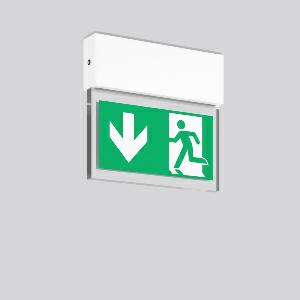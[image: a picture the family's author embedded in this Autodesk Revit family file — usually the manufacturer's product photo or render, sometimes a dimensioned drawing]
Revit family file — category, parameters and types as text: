
# Revit family: halyxx_671736_002_1_639e
name_source: partatom
category: Lighting Fixtures
units: mm (PartAtom-declared; Revit-internal decimal feet)

## family parameters
Cut with Voids When Loaded = No
Host = Face
Light Source = No
Part Type = Normal
Room Calculation Point = No
Round Connector Dimension = Use Diameter
Shared = No

## types (1)
- HALYXX (1 x LED Modul 840, 60 lm, 4000)
    Apparent Load = 2 VA
    Approval mark = CE
    CIE Flux Codes = 18 46 76 54 100
    Color Rendering = 80
    Color Temperature = 4000
    Default Elevation = 1800 mm
    Description = Series: HALYXX
Luminaire for escape route identification. Housing: extruded aluminium profile, anodised or powder-coated. Display panel: highly transparent panel, plastic, with legend on one side/both sides. Driver integrated. Suitable for connection to central battery systems. Please indicate legend number when placing your order! 
Colour: white
Length: 235 mm
Width: 40 mm
Height: 220 mm
Weight: 1.33 kg
Operating mode: maintained power mode
Viewing Distance: 19 m
Lamp: LED
Socket: without socket
Colour temperature: 4000K
Colour rendering index (CRI): 80
System power: 2 W
Rated luminous flux: 60 lm
Luminous flux, emergency: 60
System power, emergency: 1.8 W
Control gear: Regulated power supply
Protection class: I
Type of protection: IP 40
    Height = 220 mm
    Lamp = 1 x LED Modul 840
    Lamp Light Flux = 60 lm
    Lamp count = 1
    Length = 235 mm
    Lifetime = 50000 h
    Luminous efficacy = 30 lm/W
    Manufacturer = RZB
    ModVariant = No
    Model = 671736.002.1
    Mounting Place = Ceiling
    Mounting Type = Surface mounted
    Number of Poles = 1
    OnlyDefault = Yes
    Power Factor = 1
    Product Name = HALYXX
    Product group = Surface mounted ceiling luminaires
    ProductGroupID = 303
    Protection Class = Protection class I
    Protection Degree = IP 40
    RLX_Detail_Level = 1
    RLX_Emergency_Light_Flux = 60 lm
    RLX_Emergency_Type = 3
    RLX_Emergency_Type_DB = Yes
    RlxData = <blob elided: 40669 chars, md5=29793ced>
    Socket = socket
    Standby Power = 0 W
    System Light Flux = 60 lm
    System Power = 2 W
    Type Comments = Product without accessories
    Type Image = 671742.002.jpg
    URL = http://relux.com
    VarID = ---
    Voltage = 230 V
    Voltage Range = 220-240 V
    Weight = 0.00 kg
    Width = 40 mm  [stored 0.131234 ft]

note: [stored X ft] marks values corroborated as IEEE doubles in the binary element streams (Revit-internal decimal feet)

## geometry (parser evidence)
native form markers: Blend x4, Sweep x14
no freeform markers — native parametric forms only
